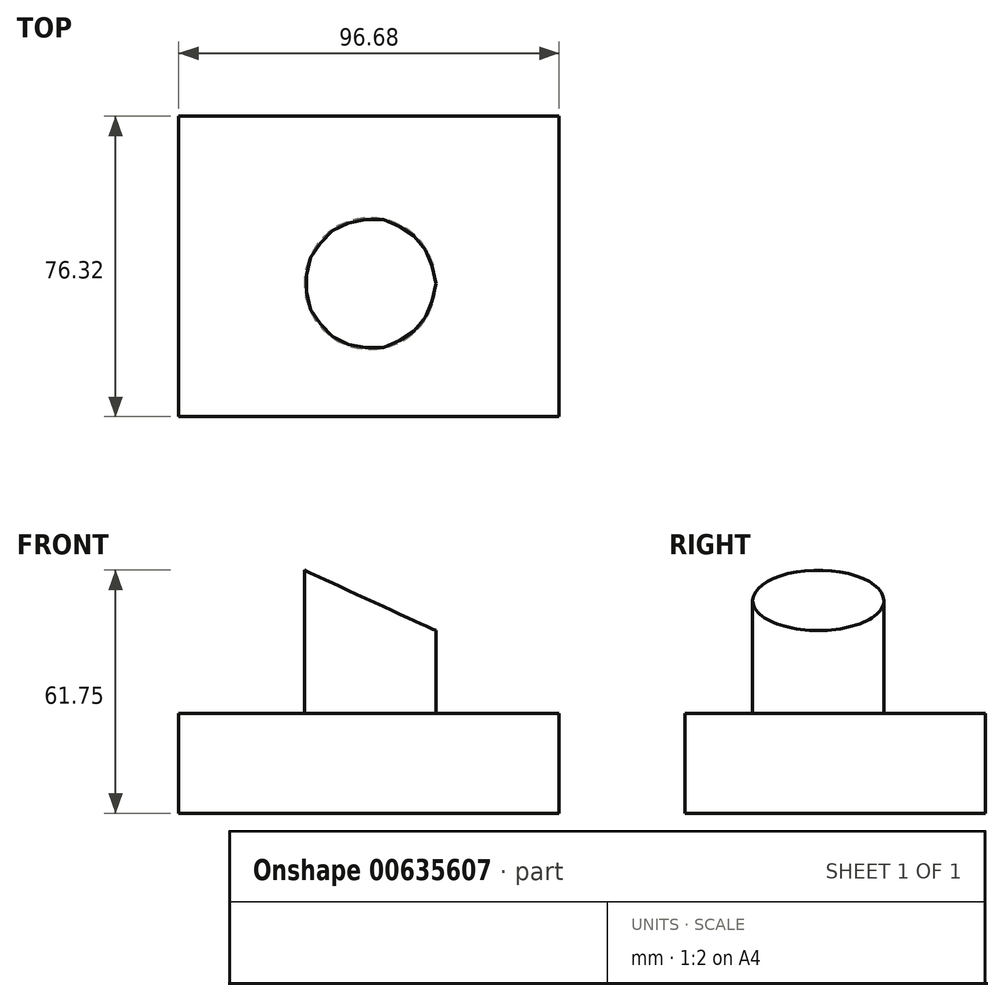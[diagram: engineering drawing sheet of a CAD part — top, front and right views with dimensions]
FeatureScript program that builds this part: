
annotation { "Feature Type Name" : "Feature", "Feature Type Description" : "" }
export const myFeature = defineFeature(function(context is Context, id is Id, definition is map)
    precondition{}
    {
        {
            var Q0;
            Q0=qCreatedBy(makeId("Top.planeOp"),FACE);
            var sketch = newSketch(context, id + "F0", { "sketchPlane" : qUnion([Q0])});
            skLineSegment(sketch, "E0.bottom", {"start": v(48.04, 42.5) * mm, "end": v(-48.64, 42.5) * mm});
            skLineSegment(sketch, "E0.top", {"start": v(48.04, -33.82) * mm, "end": v(-48.64, -33.82) * mm});
            skLineSegment(sketch, "E0.left", {"start": v(48.04, 42.5) * mm, "end": v(48.04, -33.82) * mm});
            skLineSegment(sketch, "E0.right", {"start": v(-48.64, 42.5) * mm, "end": v(-48.64, -33.82) * mm});
            skSolve(sketch);
        }
        {
            var Q0;
            Q0 = qSketchRegion(id + "F0", true);
            extrude(context, id + "F1", {"entities" : qUnion([Q0]), "depth" : 25.4 * mm, "offsetDistance" : 25.4 * mm});
        }
        {
            var Q0;
            Q0=makeQuery(id+"F1.opExtrude","CAP_FACE",FACE,{"disambiguationData":[OSD([sQuery(id+"F0.wireOp",EDGE,"E0.bottom"),sQuery(id+"F0.wireOp",EDGE,"E0.top"),sQuery(id+"F0.wireOp",EDGE,"E0.left"),sQuery(id+"F0.wireOp",EDGE,"E0.right")])],"isStart":false});
            var sketch = newSketch(context, id + "F2", { "sketchPlane" : qUnion([Q0])});
            skCircle(sketch, "E1", {"center": v(0, 0) * mm, "radius": 16.7 * mm});
            skSolve(sketch);
        }
        {
            var Q0;
            Q0=makeQuery(id+"F2.imprint","IMPRINT",FACE,{"disambiguationData":[TD([[makeQuery(id+"F2.imprint","IMPRINT",EDGE,{"derivedFrom":sQuery(id+"F2.wireOp",EDGE,"E1")}),1.0]])]});
            extrude(context, id + "F3", {"entities" : qUnion([Q0]), "operationType" : NewBodyOperationType.ADD, "depth" : 38.1 * mm, "offsetDistance" : 25.4 * mm});
        }
        {
            var Q0;
            Q0=qCreatedBy(makeId("Front.planeOp"),FACE);
            var sketch = newSketch(context, id + "F4", { "sketchPlane" : qUnion([Q0])});
            skLineSegment(sketch, "E2", {"start": v(-32.78, 69.14) * mm, "end": v(41.46, 69.14) * mm});
            skLineSegment(sketch, "E3", {"start": v(41.46, 69.14) * mm, "end": v(41.46, 35.02) * mm});
            skLineSegment(sketch, "E4", {"start": v(41.46, 35.02) * mm, "end": v(-32.78, 69.14) * mm});
            skSolve(sketch);
        }
        {
            var Q0;
            Q0 = qSketchRegion(id + "F4", true);
            extrude(context, id + "F5", {"entities" : qUnion([Q0]), "operationType" : NewBodyOperationType.REMOVE, "endBound" : BoundingType.SYMMETRIC, "oppositeDirection" : true, "depth" : 76.2 * mm, "offsetDistance" : 25.4 * mm});
        }
    });
